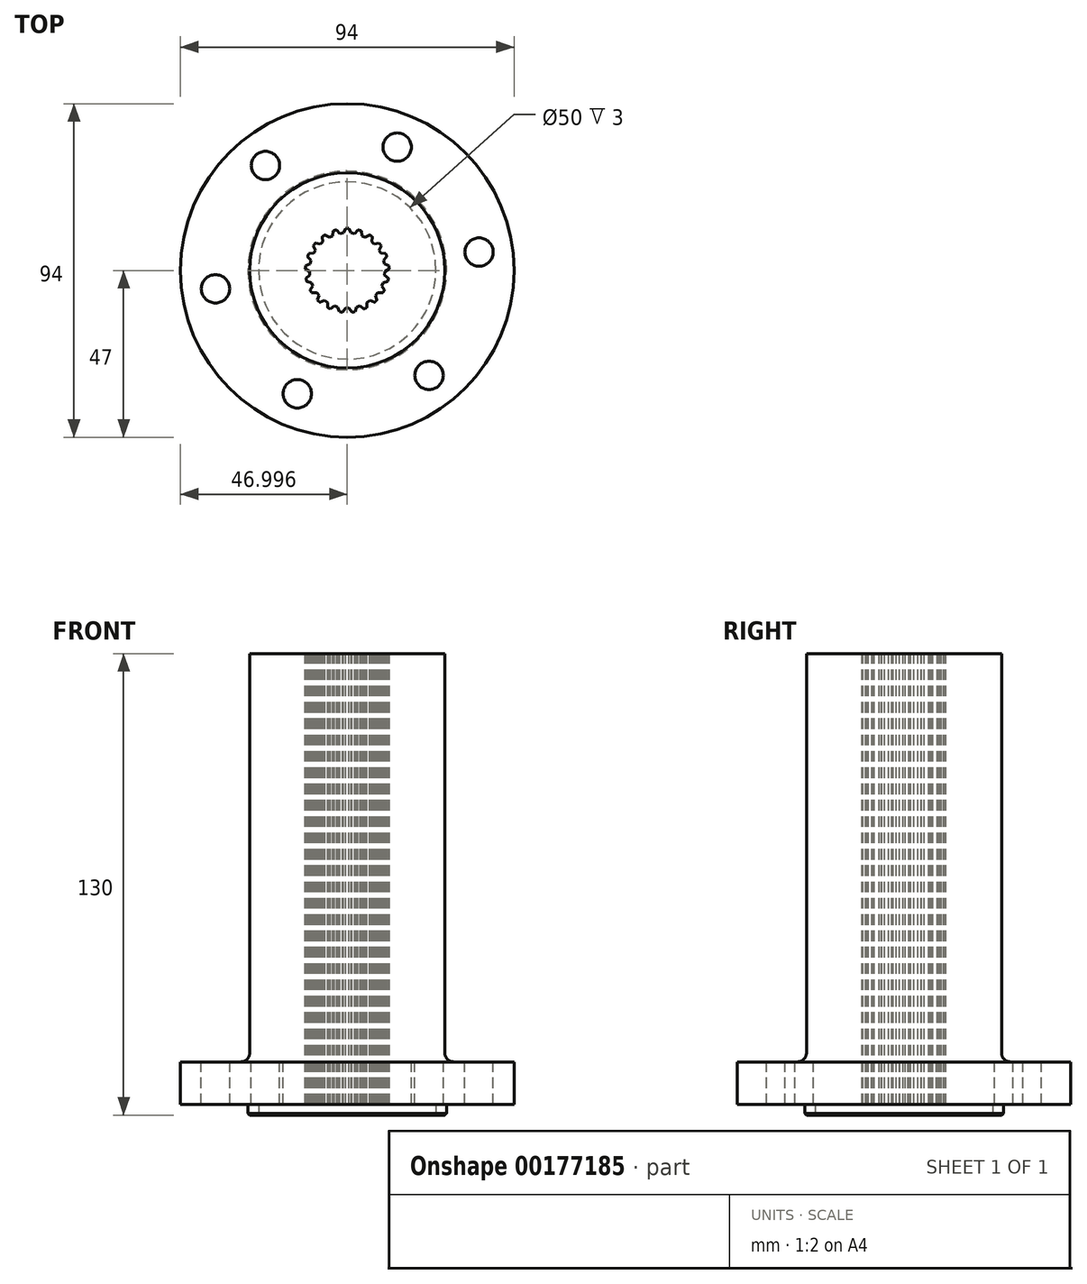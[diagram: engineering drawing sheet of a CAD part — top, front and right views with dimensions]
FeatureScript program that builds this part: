
annotation { "Feature Type Name" : "Feature", "Feature Type Description" : "" }
export const myFeature = defineFeature(function(context is Context, id is Id, definition is map)
    precondition{}
    {
        {
            var Q0;
            Q0=qCreatedBy(makeId("Front.planeOp"),FACE);
            var sketch = newSketch(context, id + "F0", { "sketchPlane" : qUnion([Q0])});
            skLineSegment(sketch, "E0", {"start": v(99.7, 60.7) * mm, "end": v(99.7, -69.3) * mm});
            skLineSegment(sketch, "E1", {"start": v(99.7, -69.3) * mm, "end": v(127.7, -69.3) * mm});
            skLineSegment(sketch, "E2", {"start": v(127.7, -69.3) * mm, "end": v(127.7, -66.3) * mm});
            skLineSegment(sketch, "E3", {"start": v(127.7, -66.3) * mm, "end": v(146.7, -66.3) * mm});
            skLineSegment(sketch, "E4", {"start": v(146.7, -66.3) * mm, "end": v(146.7, -54.3) * mm});
            skLineSegment(sketch, "E5", {"start": v(146.7, -54.3) * mm, "end": v(127.2, -54.3) * mm});
            skLineSegment(sketch, "E6", {"start": v(127.2, -54.3) * mm, "end": v(127.2, 60.7) * mm});
            skLineSegment(sketch, "E7", {"start": v(127.2, 60.7) * mm, "end": v(99.7, 60.7) * mm});
            skSolve(sketch);
        }
        {
            var Q0;
            Q0=makeQuery(id+"F0.imprint","IMPRINT",FACE,{"disambiguationData":[TD([[makeQuery(id+"F0.imprint","IMPRINT",EDGE,{"derivedFrom":sQuery(id+"F0.wireOp",EDGE,"E0")}),1.0]])]});
            var Q1;
            Q1=sQuery(id+"F0.wireOp",EDGE,"E0");
            revolve(context, id + "F1", {"surfaceOperationType" : NewSurfaceOperationType.NEW, "entities" : qUnion([Q0]), "axis" : qUnion([Q1]), "revolveType" : RevolveType.FULL});
        }
        {
            var Q0;
            Q0=makeQuery(id+"F1.opRevolve","SWEPT_FACE",FACE,{"disambiguationData":[OSD([sQuery(id+"F0.wireOp",EDGE,"E7")])]});
            var sketch = newSketch(context, id + "F2", { "sketchPlane" : qUnion([Q0])});
            skArc(sketch, "E8", {"start": v(96.68, 11.44) * mm, "mid": v(96.22, 11.3) * mm, "end": v(95.76, 11.15) * mm});
            skArc(sketch, "E9", {"start": v(110.16, 1.9) * mm, "mid": v(110.06, 2.36) * mm, "end": v(109.94, 2.83) * mm});
            skLineSegment(sketch, "E10", {"start": v(99.23, -10.6) * mm, "end": v(98.42, -11.76) * mm});
            skLineSegment(sketch, "E11", {"start": v(100.19, -10.6) * mm, "end": v(101, -11.76) * mm});
            skLineSegment(sketch, "E12", {"start": v(99.23, -10.6) * mm, "end": v(100.19, -10.6) * mm});
            skLineSegment(sketch, "E13", {"start": v(98.42, -11.76) * mm, "end": v(101, -11.76) * mm});
            skPoint(sketch, "E14", {"position": v(99.7, -10.6) * mm});
            skPoint(sketch, "E15", {"position": v(99.7, -11.76) * mm});
            skLineSegment(sketch, "E16.1.0", {"start": v(102.37, -10.28) * mm, "end": v(103.3, -10) * mm});
            skLineSegment(sketch, "E16.1.1", {"start": v(103.3, -10) * mm, "end": v(104.4, -10.86) * mm});
            skLineSegment(sketch, "E16.1.2", {"start": v(102.37, -10.28) * mm, "end": v(101.94, -11.62) * mm});
            skLineSegment(sketch, "E16.1.3", {"start": v(101.94, -11.62) * mm, "end": v(104.4, -10.86) * mm});
            skLineSegment(sketch, "E16.2.0", {"start": v(105.29, -9.04) * mm, "end": v(106.08, -8.5) * mm});
            skLineSegment(sketch, "E16.2.1", {"start": v(106.08, -8.5) * mm, "end": v(107.4, -9) * mm});
            skLineSegment(sketch, "E16.2.2", {"start": v(105.29, -9.04) * mm, "end": v(105.27, -10.44) * mm});
            skLineSegment(sketch, "E16.2.3", {"start": v(105.27, -10.44) * mm, "end": v(107.4, -9) * mm});
            skLineSegment(sketch, "E16.3.0", {"start": v(107.7, -6.99) * mm, "end": v(108.3, -6.24) * mm});
            skLineSegment(sketch, "E16.3.1", {"start": v(108.3, -6.24) * mm, "end": v(109.7, -6.33) * mm});
            skLineSegment(sketch, "E16.3.2", {"start": v(107.7, -6.99) * mm, "end": v(108.1, -8.34) * mm});
            skLineSegment(sketch, "E16.3.3", {"start": v(108.1, -8.34) * mm, "end": v(109.7, -6.33) * mm});
            skLineSegment(sketch, "E16.4.0", {"start": v(109.4, -4.32) * mm, "end": v(109.76, -3.43) * mm});
            skLineSegment(sketch, "E16.4.1", {"start": v(109.76, -3.43) * mm, "end": v(111.12, -3.1) * mm});
            skLineSegment(sketch, "E16.4.2", {"start": v(109.4, -4.32) * mm, "end": v(110.18, -5.5) * mm});
            skLineSegment(sketch, "E16.4.3", {"start": v(110.18, -5.5) * mm, "end": v(111.12, -3.1) * mm});
            skLineSegment(sketch, "E16.5.0", {"start": v(110.25, -1.27) * mm, "end": v(110.32, -0.31) * mm});
            skLineSegment(sketch, "E16.5.1", {"start": v(110.32, -0.31) * mm, "end": v(111.53, 0.4) * mm});
            skLineSegment(sketch, "E16.5.2", {"start": v(110.25, -1.27) * mm, "end": v(111.34, -2.16) * mm});
            skLineSegment(sketch, "E16.5.3", {"start": v(111.34, -2.16) * mm, "end": v(111.53, 0.4) * mm});
            skLineSegment(sketch, "E16.6.0", {"start": v(110.16, 1.9) * mm, "end": v(109.94, 2.83) * mm});
            skLineSegment(sketch, "E16.6.1", {"start": v(109.94, 2.83) * mm, "end": v(110.88, 3.87) * mm});
            skLineSegment(sketch, "E16.6.2", {"start": v(110.16, 1.9) * mm, "end": v(111.46, 1.36) * mm});
            skLineSegment(sketch, "E16.6.3", {"start": v(111.46, 1.36) * mm, "end": v(110.88, 3.87) * mm});
            skLineSegment(sketch, "E16.7.0", {"start": v(109.13, 4.89) * mm, "end": v(108.65, 5.72) * mm});
            skLineSegment(sketch, "E16.7.1", {"start": v(108.65, 5.72) * mm, "end": v(109.25, 7) * mm});
            skLineSegment(sketch, "E16.7.2", {"start": v(109.13, 4.89) * mm, "end": v(110.53, 4.77) * mm});
            skLineSegment(sketch, "E16.8.0", {"start": v(107.27, 7.45) * mm, "end": v(106.57, 8.1) * mm});
            skLineSegment(sketch, "E16.8.1", {"start": v(106.57, 8.1) * mm, "end": v(106.76, 9.5) * mm});
            skLineSegment(sketch, "E16.8.2", {"start": v(107.27, 7.45) * mm, "end": v(108.65, 7.75) * mm});
            skLineSegment(sketch, "E16.9.0", {"start": v(104.74, 9.35) * mm, "end": v(103.88, 9.77) * mm});
            skLineSegment(sketch, "E16.9.1", {"start": v(103.88, 9.77) * mm, "end": v(103.65, 11.15) * mm});
            skLineSegment(sketch, "E16.9.2", {"start": v(104.74, 9.35) * mm, "end": v(105.97, 10.04) * mm});
            skLineSegment(sketch, "E16.10.0", {"start": v(101.76, 10.42) * mm, "end": v(100.81, 10.56) * mm});
            skLineSegment(sketch, "E16.10.1", {"start": v(100.81, 10.56) * mm, "end": v(100.19, 11.82) * mm});
            skLineSegment(sketch, "E16.10.2", {"start": v(101.76, 10.42) * mm, "end": v(102.73, 11.44) * mm});
            skLineSegment(sketch, "E16.11.0", {"start": v(98.6, 10.56) * mm, "end": v(97.65, 10.42) * mm});
            skLineSegment(sketch, "E16.11.1", {"start": v(97.65, 10.42) * mm, "end": v(96.68, 11.44) * mm});
            skLineSegment(sketch, "E16.11.2", {"start": v(98.6, 10.56) * mm, "end": v(99.23, 11.82) * mm});
            skLineSegment(sketch, "E16.12.0", {"start": v(95.54, 9.77) * mm, "end": v(94.67, 9.35) * mm});
            skLineSegment(sketch, "E16.12.1", {"start": v(94.67, 9.35) * mm, "end": v(93.44, 10.04) * mm});
            skLineSegment(sketch, "E16.12.2", {"start": v(95.54, 9.77) * mm, "end": v(95.76, 11.15) * mm});
            skLineSegment(sketch, "E16.12.3", {"start": v(95.76, 11.15) * mm, "end": v(93.44, 10.04) * mm});
            skLineSegment(sketch, "E16.13.0", {"start": v(92.84, 8.1) * mm, "end": v(92.14, 7.45) * mm});
            skLineSegment(sketch, "E16.13.1", {"start": v(92.14, 7.45) * mm, "end": v(90.76, 7.75) * mm});
            skLineSegment(sketch, "E16.13.2", {"start": v(92.84, 8.1) * mm, "end": v(92.65, 9.5) * mm});
            skLineSegment(sketch, "E16.13.3", {"start": v(92.65, 9.5) * mm, "end": v(90.76, 7.75) * mm});
            skLineSegment(sketch, "E16.14.0", {"start": v(90.76, 5.72) * mm, "end": v(90.28, 4.89) * mm});
            skLineSegment(sketch, "E16.14.1", {"start": v(90.28, 4.89) * mm, "end": v(88.88, 4.77) * mm});
            skLineSegment(sketch, "E16.14.2", {"start": v(90.76, 5.72) * mm, "end": v(90.17, 7) * mm});
            skLineSegment(sketch, "E16.14.3", {"start": v(90.17, 7) * mm, "end": v(88.88, 4.77) * mm});
            skLineSegment(sketch, "E16.15.0", {"start": v(89.47, 2.83) * mm, "end": v(89.26, 1.9) * mm});
            skLineSegment(sketch, "E16.15.1", {"start": v(89.26, 1.9) * mm, "end": v(87.95, 1.36) * mm});
            skLineSegment(sketch, "E16.15.2", {"start": v(89.47, 2.83) * mm, "end": v(88.53, 3.87) * mm});
            skLineSegment(sketch, "E16.15.3", {"start": v(88.53, 3.87) * mm, "end": v(87.95, 1.36) * mm});
            skLineSegment(sketch, "E16.16.0", {"start": v(89.1, -0.31) * mm, "end": v(89.16, -1.27) * mm});
            skLineSegment(sketch, "E16.16.1", {"start": v(89.16, -1.27) * mm, "end": v(88.08, -2.16) * mm});
            skLineSegment(sketch, "E16.16.2", {"start": v(89.1, -0.31) * mm, "end": v(87.88, 0.4) * mm});
            skLineSegment(sketch, "E16.16.3", {"start": v(87.88, 0.4) * mm, "end": v(88.08, -2.16) * mm});
            skLineSegment(sketch, "E16.17.0", {"start": v(89.65, -3.43) * mm, "end": v(90, -4.32) * mm});
            skLineSegment(sketch, "E16.17.1", {"start": v(90, -4.32) * mm, "end": v(89.23, -5.5) * mm});
            skLineSegment(sketch, "E16.17.2", {"start": v(89.65, -3.43) * mm, "end": v(88.29, -3.1) * mm});
            skLineSegment(sketch, "E16.17.3", {"start": v(88.29, -3.1) * mm, "end": v(89.23, -5.5) * mm});
            skLineSegment(sketch, "E16.18.0", {"start": v(91.11, -6.24) * mm, "end": v(91.71, -6.99) * mm});
            skLineSegment(sketch, "E16.18.1", {"start": v(91.71, -6.99) * mm, "end": v(91.31, -8.34) * mm});
            skLineSegment(sketch, "E16.18.2", {"start": v(91.11, -6.24) * mm, "end": v(89.7, -6.33) * mm});
            skLineSegment(sketch, "E16.18.3", {"start": v(89.7, -6.33) * mm, "end": v(91.31, -8.34) * mm});
            skLineSegment(sketch, "E16.19.0", {"start": v(93.33, -8.5) * mm, "end": v(94.13, -9.04) * mm});
            skLineSegment(sketch, "E16.19.1", {"start": v(94.13, -9.04) * mm, "end": v(94.14, -10.44) * mm});
            skLineSegment(sketch, "E16.19.2", {"start": v(93.33, -8.5) * mm, "end": v(92.02, -9) * mm});
            skLineSegment(sketch, "E16.19.3", {"start": v(92.02, -9) * mm, "end": v(94.14, -10.44) * mm});
            skLineSegment(sketch, "E16.20.0", {"start": v(96.12, -10) * mm, "end": v(97.04, -10.28) * mm});
            skLineSegment(sketch, "E16.20.1", {"start": v(97.04, -10.28) * mm, "end": v(97.47, -11.62) * mm});
            skLineSegment(sketch, "E16.20.2", {"start": v(96.12, -10) * mm, "end": v(95, -10.86) * mm});
            skLineSegment(sketch, "E16.20.3", {"start": v(95, -10.86) * mm, "end": v(97.47, -11.62) * mm});
            skArc(sketch, "E17.trimOffspring", {"start": v(110.25, -1.27) * mm, "mid": v(110.3, -0.8) * mm, "end": v(110.32, -0.31) * mm});
            skArc(sketch, "E18.trimOffspring", {"start": v(109.4, -4.32) * mm, "mid": v(109.6, -3.88) * mm, "end": v(109.76, -3.43) * mm});
            skArc(sketch, "E19.trimOffspring", {"start": v(107.7, -6.99) * mm, "mid": v(108, -6.62) * mm, "end": v(108.3, -6.24) * mm});
            skArc(sketch, "E20.trimOffspring", {"start": v(105.29, -9.04) * mm, "mid": v(105.69, -8.77) * mm, "end": v(106.08, -8.5) * mm});
            skArc(sketch, "E21.trimOffspring", {"start": v(102.37, -10.28) * mm, "mid": v(102.84, -10.15) * mm, "end": v(103.3, -10) * mm});
            skArc(sketch, "E22.trimOffspring", {"start": v(99.23, -10.6) * mm, "mid": v(99.7, -10.62) * mm, "end": v(100.19, -10.6) * mm});
            skArc(sketch, "E23.trimOffspring", {"start": v(96.12, -10) * mm, "mid": v(96.58, -10.15) * mm, "end": v(97.04, -10.28) * mm});
            skArc(sketch, "E24.trimOffspring", {"start": v(109.13, 4.89) * mm, "mid": v(108.9, 5.3) * mm, "end": v(108.65, 5.72) * mm});
            skArc(sketch, "E25.trimOffspring", {"start": v(107.27, 7.45) * mm, "mid": v(106.93, 7.79) * mm, "end": v(106.57, 8.1) * mm});
            skArc(sketch, "E26.trimOffspring", {"start": v(93.33, -8.5) * mm, "mid": v(93.72, -8.77) * mm, "end": v(94.13, -9.04) * mm});
            skArc(sketch, "E27.trimOffspring", {"start": v(91.11, -6.24) * mm, "mid": v(91.4, -6.62) * mm, "end": v(91.71, -6.99) * mm});
            skArc(sketch, "E28.trimOffspring", {"start": v(89.65, -3.43) * mm, "mid": v(89.82, -3.88) * mm, "end": v(90, -4.32) * mm});
            skArc(sketch, "E29.trimOffspring", {"start": v(89.1, -0.31) * mm, "mid": v(89.12, -0.8) * mm, "end": v(89.16, -1.27) * mm});
            skArc(sketch, "E30.trimOffspring", {"start": v(89.47, 2.83) * mm, "mid": v(89.35, 2.36) * mm, "end": v(89.26, 1.9) * mm});
            skArc(sketch, "E31.trimOffspring", {"start": v(90.76, 5.72) * mm, "mid": v(90.5, 5.3) * mm, "end": v(90.28, 4.89) * mm});
            skArc(sketch, "E32.trimOffspring", {"start": v(92.84, 8.1) * mm, "mid": v(92.48, 7.79) * mm, "end": v(92.14, 7.45) * mm});
            skArc(sketch, "E33.trimOffspring", {"start": v(95.54, 9.77) * mm, "mid": v(95.1, 9.57) * mm, "end": v(94.67, 9.35) * mm});
            skArc(sketch, "E34.trimOffspring", {"start": v(98.6, 10.56) * mm, "mid": v(98.12, 10.5) * mm, "end": v(97.65, 10.42) * mm});
            skArc(sketch, "E35.trimOffspring", {"start": v(101.76, 10.42) * mm, "mid": v(101.29, 10.5) * mm, "end": v(100.81, 10.56) * mm});
            skArc(sketch, "E36.trimOffspring", {"start": v(104.74, 9.35) * mm, "mid": v(104.31, 9.57) * mm, "end": v(103.88, 9.77) * mm});
            skArc(sketch, "E37.trimOffspring", {"start": v(100.19, 11.82) * mm, "mid": v(99.7, 11.83) * mm, "end": v(99.23, 11.82) * mm});
            skArc(sketch, "E38.trimOffspring", {"start": v(103.65, 11.15) * mm, "mid": v(103.2, 11.3) * mm, "end": v(102.73, 11.44) * mm});
            skArc(sketch, "E39.trimOffspring", {"start": v(106.76, 9.5) * mm, "mid": v(106.37, 9.77) * mm, "end": v(105.97, 10.04) * mm});
            skArc(sketch, "E40.trimOffspring", {"start": v(109.25, 7) * mm, "mid": v(108.95, 7.38) * mm, "end": v(108.65, 7.75) * mm});
            skArc(sketch, "E41.trimOffspring", {"start": v(93.44, 10.04) * mm, "mid": v(96.22, -11.3) * mm, "end": v(110.53, 4.77) * mm});
            skSolve(sketch);
        }
        {
            var Q0;
            Q0=makeQuery(id+"F2.imprint","IMPRINT",FACE,{"disambiguationData":[TD([[makeQuery(id+"F2.imprint","IMPRINT",EDGE,{"derivedFrom":sQuery(id+"F2.wireOp",EDGE,"E8")}),1.0]])]});
            extrude(context, id + "F3", {"entities" : qUnion([Q0]), "operationType" : NewBodyOperationType.REMOVE, "oppositeDirection" : true, "depth" : 241 * mm, "offsetDistance" : 25 * mm});
        }
        {
            var Q0;
            Q0=makeQuery(id+"F1.opRevolve","SWEPT_FACE",FACE,{"disambiguationData":[OSD([sQuery(id+"F0.wireOp",EDGE,"E5")])]});
            var sketch = newSketch(context, id + "F4", { "sketchPlane" : qUnion([Q0])});
            skCircle(sketch, "E42", {"center": v(85.62, -34.75) * mm, "radius": 4 * mm});
            skCircle(sketch, "E43.1.0", {"center": v(122.76, -29.57) * mm, "radius": 4 * mm});
            skCircle(sketch, "E43.2.0", {"center": v(136.85, 5.18) * mm, "radius": 4 * mm});
            skCircle(sketch, "E43.3.0", {"center": v(113.79, 34.75) * mm, "radius": 4 * mm});
            skCircle(sketch, "E43.4.0", {"center": v(76.65, 29.57) * mm, "radius": 4 * mm});
            skCircle(sketch, "E43.5.0", {"center": v(62.57, -5.18) * mm, "radius": 4 * mm});
            skPoint(sketch, "E43.center", {"position": v(99.7, 0) * mm});
            skSolve(sketch);
        }
        {
            var Q0;
            Q0=makeQuery(id+"F4.imprint","IMPRINT",FACE,{"disambiguationData":[TD([[makeQuery(id+"F4.imprint","IMPRINT",EDGE,{"derivedFrom":sQuery(id+"F4.wireOp",EDGE,"E42")}),1.0]])]});
            var Q1;
            Q1=makeQuery(id+"F4.imprint","IMPRINT",FACE,{"disambiguationData":[TD([[makeQuery(id+"F4.imprint","IMPRINT",EDGE,{"derivedFrom":sQuery(id+"F4.wireOp",EDGE,"E43.1.0")}),1.0]])]});
            var Q2;
            Q2=makeQuery(id+"F4.imprint","IMPRINT",FACE,{"disambiguationData":[TD([[makeQuery(id+"F4.imprint","IMPRINT",EDGE,{"derivedFrom":sQuery(id+"F4.wireOp",EDGE,"E43.2.0")}),1.0]])]});
            var Q3;
            Q3=makeQuery(id+"F4.imprint","IMPRINT",FACE,{"disambiguationData":[TD([[makeQuery(id+"F4.imprint","IMPRINT",EDGE,{"derivedFrom":sQuery(id+"F4.wireOp",EDGE,"E43.3.0")}),1.0]])]});
            var Q4;
            Q4=makeQuery(id+"F4.imprint","IMPRINT",FACE,{"disambiguationData":[TD([[makeQuery(id+"F4.imprint","IMPRINT",EDGE,{"derivedFrom":sQuery(id+"F4.wireOp",EDGE,"E43.4.0")}),1.0]])]});
            var Q5;
            Q5=makeQuery(id+"F4.imprint","IMPRINT",FACE,{"disambiguationData":[TD([[makeQuery(id+"F4.imprint","IMPRINT",EDGE,{"derivedFrom":sQuery(id+"F4.wireOp",EDGE,"E43.5.0")}),1.0]])]});
            extrude(context, id + "F5", {"entities" : qUnion([Q0, Q1, Q2, Q3, Q4, Q5]), "operationType" : NewBodyOperationType.REMOVE, "oppositeDirection" : true, "depth" : 25 * mm, "offsetDistance" : 25 * mm});
        }
        {
            var Q0;
            Q0=makeQuery(id+"F1.opRevolve","SWEPT_EDGE",EDGE,{"disambiguationData":[OSD([sQuery(id+"F0.wireOp",EDGE,"E5"),sQuery(id+"F0.wireOp",EDGE,"E6")])]});
            fillet(context, id + "F6", {"entities" : qUnion([Q0]), "radius" : 2.5 * mm, "tangentPropagation" : true, "allowEdgeOverflow" : false});
        }
        {
            var Q0;
            Q0=makeQuery(id+"F1.opRevolve","SWEPT_FACE",FACE,{"disambiguationData":[OSD([sQuery(id+"F0.wireOp",EDGE,"E1")])]});
            var sketch = newSketch(context, id + "F7", { "sketchPlane" : qUnion([Q0])});
            skCircle(sketch, "E44", {"center": v(99.7, 0) * mm, "radius": 25 * mm});
            skSolve(sketch);
        }
        {
            var Q0;
            Q0=makeQuery(id+"F7.imprint","IMPRINT",FACE,{"disambiguationData":[TD([[makeQuery(id+"F7.imprint","IMPRINT",EDGE,{"derivedFrom":sQuery(id+"F7.wireOp",EDGE,"E44")}),1.0]])]});
            extrude(context, id + "F8", {"entities" : qUnion([Q0]), "operationType" : NewBodyOperationType.REMOVE, "oppositeDirection" : true, "depth" : 3 * mm, "offsetDistance" : 25 * mm});
        }
        {
            var Q0;
            Q0=makeQuery(id+"F1.opRevolve","SWEPT_EDGE",EDGE,{"disambiguationData":[OSD([sQuery(id+"F0.wireOp",EDGE,"E1"),sQuery(id+"F0.wireOp",EDGE,"E2")])]});
            chamfer(context, id + "F9", {"entities" : qUnion([Q0]), "chamferType" : ChamferType.OFFSET_ANGLE, "width" : 0.5 * mm, "oppositeDirection" : false, "angle" : 45 * degree, "tangentPropagation" : true});
        }
    });
